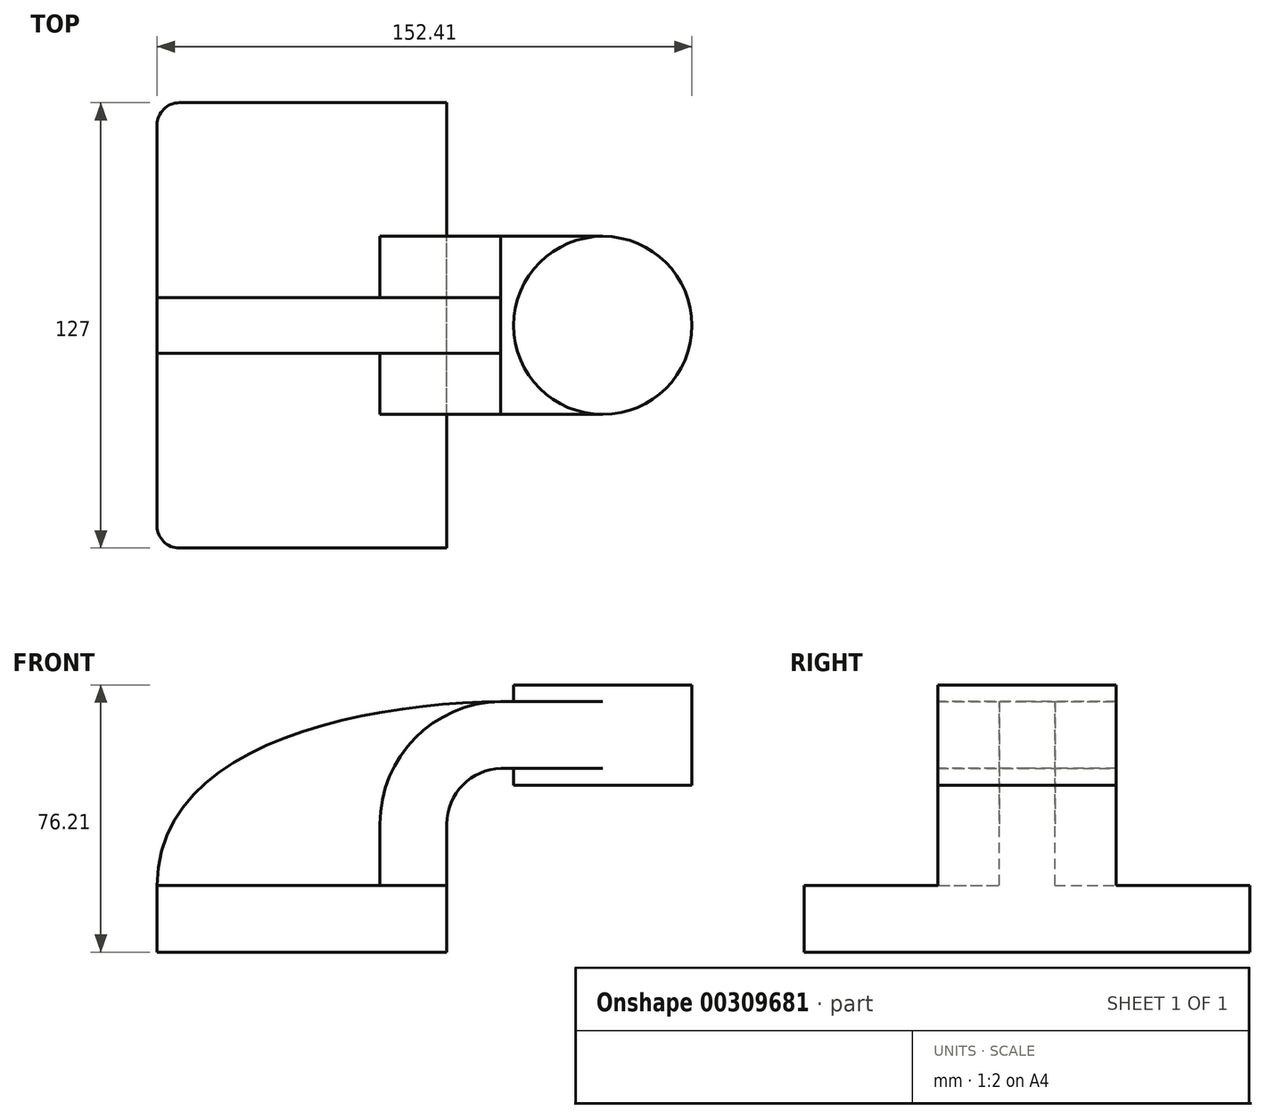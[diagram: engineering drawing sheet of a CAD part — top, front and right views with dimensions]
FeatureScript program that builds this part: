
annotation { "Feature Type Name" : "Feature", "Feature Type Description" : "" }
export const myFeature = defineFeature(function(context is Context, id is Id, definition is map)
    precondition{}
    {
        {
            var Q0;
            Q0=qCreatedBy(makeId("Front.planeOp"),FACE);
            var sketch = newSketch(context, id + "F0", { "sketchPlane" : qUnion([Q0])});
            skLineSegment(sketch, "E0.bottom", {"start": v(41.28, -9.52) * mm, "end": v(-41.28, -9.53) * mm});
            skLineSegment(sketch, "E0.top", {"start": v(41.27, 9.53) * mm, "end": v(-41.28, 9.52) * mm});
            skLineSegment(sketch, "E0.left", {"start": v(41.28, -9.53) * mm, "end": v(41.28, 9.53) * mm});
            skLineSegment(sketch, "E0.right", {"start": v(-41.28, -9.53) * mm, "end": v(-41.28, 9.52) * mm});
            skPoint(sketch, "E0.middle", {"position": v(0, 0) * mm});
            skLineSegment(sketch, "E1", {"start": v(41.28, -9.53) * mm, "end": v(41.28, 27) * mm});
            skArc(sketch, "E2", {"start": v(56.79, 42.88) * mm, "mid": v(45.8, 38.1) * mm, "end": v(41.27, 27) * mm});
            skLineSegment(sketch, "E3", {"start": v(56.79, 42.88) * mm, "end": v(85.73, 42.88) * mm});
            skLineSegment(sketch, "E4.bottom", {"start": v(111.13, 38.1) * mm, "end": v(60.33, 38.1) * mm});
            skLineSegment(sketch, "E4.top", {"start": v(111.13, 66.68) * mm, "end": v(60.33, 66.68) * mm});
            skLineSegment(sketch, "E4.left", {"start": v(111.13, 38.1) * mm, "end": v(111.13, 66.68) * mm});
            skLineSegment(sketch, "E4.right", {"start": v(60.33, 38.1) * mm, "end": v(60.33, 66.68) * mm});
            skPoint(sketch, "E4.middle", {"position": v(85.73, 52.39) * mm});
            skPoint(sketch, "E4.cornerSnap0", {"position": v(45.8, 38.1) * mm});
            skLineSegment(sketch, "E5.0", {"start": v(22.23, -9.53) * mm, "end": v(22.23, 27) * mm});
            skArc(sketch, "E5.1", {"start": v(56.6, 61.93) * mm, "mid": v(32.26, 51.5) * mm, "end": v(22.22, 27) * mm});
            skLineSegment(sketch, "E5.2", {"start": v(56.6, 61.93) * mm, "end": v(85.73, 61.93) * mm});
            skLineSegment(sketch, "E6", {"start": v(85.73, 38.1) * mm, "end": v(85.73, 66.68) * mm});
            skFitSpline(sketch, "E7", {"points": [v(-41.28, 9.52) * mm, v(56.6, 61.93) * mm], "startDerivative": vector(-0.75, 119.64) * mm, "endDerivative": vector(120.7, 1.34) * mm});
            skSolve(sketch);
        }
        {
            var Q0;
            {var subQ0=sQuery(id+"F0.wireOp",EDGE,"E0.right");Q0=makeQuery(id+"F0.imprint","IMPRINT",FACE,{"disambiguationData":[TD([[makeQuery(id+"F0.imprint","IMPRINT",EDGE,{"derivedFrom":subQ0}),-1.0]])]});}
            var Q1;
            {var subQ0=sQuery(id+"F0.wireOp",EDGE,"E1");var subQ1=sQuery(id+"F0.wireOp",EDGE,"E0.bottom");var subQ2=makeQuery(id+"F0.imprint","INTERSECT",VERTEX,{"derivedFrom":[subQ1,subQ0]});Q1=makeQuery(id+"F0.imprint","IMPRINT",FACE,{"disambiguationData":[TD([[makeQuery(id+"F0.imprint","IMPRINT",EDGE,{"disambiguationData":[TD([[subQ2,-1.0]])],"derivedFrom":subQ1}),-1.0]])]});}
            extrude(context, id + "F1", {"entities" : qUnion([Q0, Q1]), "endBound" : BoundingType.SYMMETRIC, "depth" : 127 * mm});
        }
        {
            var Q0;
            {var subQ1=sQuery(id+"F0.wireOp",EDGE,"E2");Q0=makeQuery(id+"F0.imprint","IMPRINT",FACE,{"disambiguationData":[TD([[makeQuery(id+"F0.imprint","IMPRINT",EDGE,{"derivedFrom":subQ1}),-1.0]])]});}
            var Q1;
            {var subQ0=sQuery(id+"F0.wireOp",EDGE,"E6");var subQ1=sQuery(id+"F0.wireOp",EDGE,"E3");var subQ2=makeQuery(id+"F0.imprint","INTERSECT",VERTEX,{"derivedFrom":[subQ1,subQ0]});Q1=makeQuery(id+"F0.imprint","IMPRINT",FACE,{"disambiguationData":[TD([[makeQuery(id+"F0.imprint","IMPRINT",EDGE,{"disambiguationData":[TD([[subQ2,1.0]])],"derivedFrom":subQ1}),1.0]])]});}
            extrude(context, id + "F2", {"entities" : qUnion([Q0, Q1]), "operationType" : NewBodyOperationType.ADD, "endBound" : BoundingType.SYMMETRIC, "depth" : 50.8 * mm});
        }
        {
            var Q0;
            {var subQ4=sQuery(id+"F0.wireOp",EDGE,"E5.1");Q0=makeQuery(id+"F0.imprint","IMPRINT",FACE,{"disambiguationData":[TD([[makeQuery(id+"F0.imprint","IMPRINT",EDGE,{"derivedFrom":subQ4}),-1.0]])]});}
            extrude(context, id + "F3", {"entities" : qUnion([Q0]), "operationType" : NewBodyOperationType.ADD, "endBound" : BoundingType.SYMMETRIC, "depth" : 15.88 * mm});
        }
        {
            var Q0;
            {var subQ4=sQuery(id+"F0.wireOp",EDGE,"E4.left");Q0=makeQuery(id+"F0.imprint","IMPRINT",FACE,{"disambiguationData":[TD([[makeQuery(id+"F0.imprint","IMPRINT",EDGE,{"derivedFrom":subQ4}),1.0]])]});}
            var Q1;
            Q1=sQuery(id+"F0.wireOp",EDGE,"E6");
            revolve(context, id + "F4", {"operationType" : NewBodyOperationType.ADD, "entities" : qUnion([Q0]), "axis" : qUnion([Q1]), "revolveType" : RevolveType.FULL});
        }
        {
            var Q0;
            Q0=makeQuery(id+"F1.opExtrude","CAP_EDGE",EDGE,{"disambiguationData":[OSD([sQuery(id+"F0.wireOp",EDGE,"E1")])],"isStart":false});
            var Q1;
            Q1=makeQuery(id+"F1.opExtrude","CAP_EDGE",EDGE,{"disambiguationData":[OSD([sQuery(id+"F0.wireOp",EDGE,"E0.right")])],"isStart":false});
            var Q2;
            Q2=makeQuery(id+"F1.opExtrude","CAP_EDGE",EDGE,{"disambiguationData":[OSD([sQuery(id+"F0.wireOp",EDGE,"E1")])],"isStart":true});
            var Q3;
            Q3=makeQuery(id+"F1.opExtrude","CAP_EDGE",EDGE,{"disambiguationData":[OSD([sQuery(id+"F0.wireOp",EDGE,"E0.right")])],"isStart":true});
            fillet(context, id + "F5", {"entities" : qUnion([Q0, Q1, Q2, Q3]), "radius" : 6.35 * mm, "tangentPropagation" : true, "allowEdgeOverflow" : false});
        }
    });
